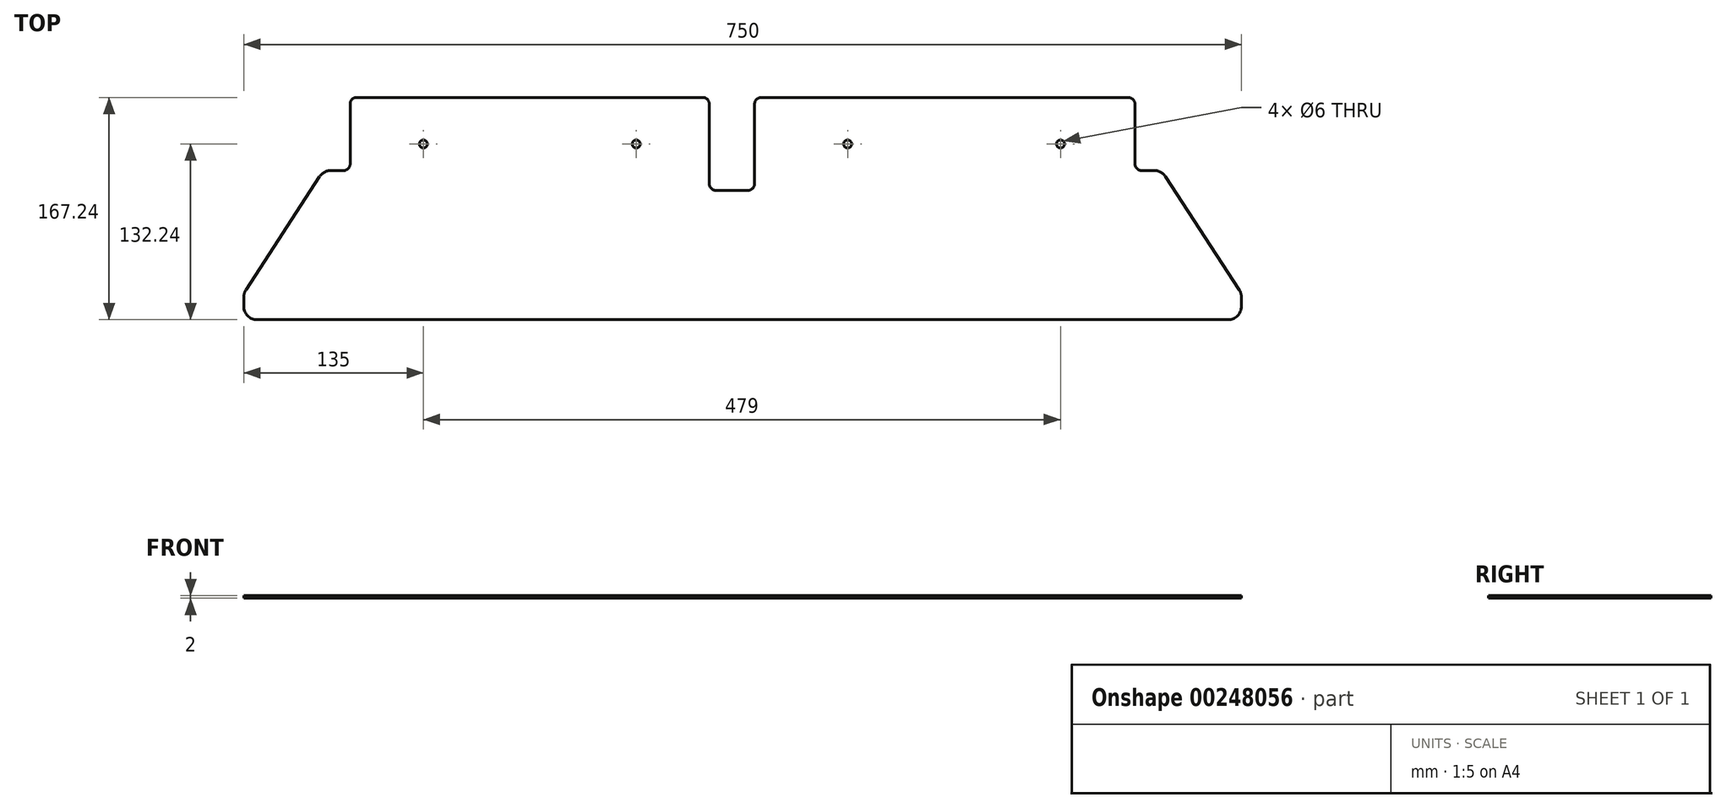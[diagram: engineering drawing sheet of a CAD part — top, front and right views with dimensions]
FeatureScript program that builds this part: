
annotation { "Feature Type Name" : "Feature", "Feature Type Description" : "" }
export const myFeature = defineFeature(function(context is Context, id is Id, definition is map)
    precondition{}
    {
        {
            var Q0;
            Q0=qCreatedBy(makeId("Top.planeOp"),FACE);
            var sketch = newSketch(context, id + "F0", { "sketchPlane" : qUnion([Q0])});
            skLineSegment(sketch, "E0.bottom", {"start": v(5, 0) * mm, "end": v(265, 0) * mm});
            skLineSegment(sketch, "E0.top", {"start": v(0, -55) * mm, "end": v(270, -55) * mm});
            skLineSegment(sketch, "E0.left", {"start": v(0, -5) * mm, "end": v(0, -50) * mm});
            skLineSegment(sketch, "E0.right", {"start": v(590, -5) * mm, "end": v(590, -50) * mm});
            skLineSegment(sketch, "E1", {"start": v(-5, -55) * mm, "end": v(-14.58, -55) * mm});
            skLineSegment(sketch, "E2", {"start": v(595, -55) * mm, "end": v(604.58, -55) * mm});
            skLineSegment(sketch, "E3", {"start": v(-70, -167.24) * mm, "end": v(660, -167.24) * mm});
            skLineSegment(sketch, "E4", {"start": v(-80, -157.24) * mm, "end": v(-80, -150.2) * mm});
            skLineSegment(sketch, "E5", {"start": v(-78.38, -144.75) * mm, "end": v(-22.96, -59.55) * mm});
            skLineSegment(sketch, "E6", {"start": v(670, -157.24) * mm, "end": v(670, -150.2) * mm});
            skLineSegment(sketch, "E7", {"start": v(612.96, -59.55) * mm, "end": v(668.38, -144.75) * mm});
            skLineSegment(sketch, "E8.top", {"start": v(275, -70) * mm, "end": v(299, -70) * mm});
            skLineSegment(sketch, "E8.left", {"start": v(270, -5) * mm, "end": v(270, -65) * mm});
            skLineSegment(sketch, "E8.right", {"start": v(304, -5) * mm, "end": v(304, -65) * mm});
            skPoint(sketch, "E9.visualSharp", {"position": v(270, -70) * mm});
            skArc(sketch, "E9.filletArc", {"start": v(270, -65) * mm, "mid": v(271.46, -68.54) * mm, "end": v(275, -70) * mm});
            skPoint(sketch, "E10.visualSharp", {"position": v(304, -70) * mm});
            skArc(sketch, "E10.filletArc", {"start": v(299, -70) * mm, "mid": v(302.54, -68.54) * mm, "end": v(304, -65) * mm});
            skLineSegment(sketch, "E11.trimOffspring", {"start": v(309, 0) * mm, "end": v(585, 0) * mm});
            skPoint(sketch, "E12.visualSharp", {"position": v(304, 0) * mm});
            skArc(sketch, "E12.filletArc", {"start": v(309, 0) * mm, "mid": v(305.46, -1.46) * mm, "end": v(304, -5) * mm});
            skPoint(sketch, "E13.visualSharp", {"position": v(270, 0) * mm});
            skArc(sketch, "E13.filletArc", {"start": v(270, -5) * mm, "mid": v(268.54, -1.46) * mm, "end": v(265, 0) * mm});
            skPoint(sketch, "E14.visualSharp", {"position": v(590, 0) * mm});
            skArc(sketch, "E14.filletArc", {"start": v(590, -5) * mm, "mid": v(588.54, -1.46) * mm, "end": v(585, 0) * mm});
            skPoint(sketch, "E15.visualSharp", {"position": v(590, -55) * mm});
            skArc(sketch, "E15.filletArc", {"start": v(590, -50) * mm, "mid": v(591.46, -53.54) * mm, "end": v(595, -55) * mm});
            skPoint(sketch, "E16.visualSharp", {"position": v(0, 0) * mm});
            skArc(sketch, "E16.filletArc", {"start": v(5, 0) * mm, "mid": v(1.46, -1.46) * mm, "end": v(0, -5) * mm});
            skPoint(sketch, "E17.visualSharp", {"position": v(0, -55) * mm});
            skArc(sketch, "E17.filletArc", {"start": v(-5, -55) * mm, "mid": v(-1.46, -53.54) * mm, "end": v(0, -50) * mm});
            skPoint(sketch, "E18.visualSharp", {"position": v(-80, -167.24) * mm});
            skArc(sketch, "E18.filletArc", {"start": v(-80, -157.24) * mm, "mid": v(-77.07, -164.31) * mm, "end": v(-70, -167.24) * mm});
            skPoint(sketch, "E19.visualSharp", {"position": v(670, -167.24) * mm});
            skArc(sketch, "E19.filletArc", {"start": v(660, -167.24) * mm, "mid": v(667.07, -164.31) * mm, "end": v(670, -157.24) * mm});
            skLineSegment(sketch, "E20", {"start": v(9.34, -35) * mm, "end": v(270, -35) * mm});
            skCircle(sketch, "E21", {"center": v(55, -35) * mm, "radius": 3 * mm});
            skCircle(sketch, "E22", {"center": v(215, -35) * mm, "radius": 3 * mm});
            skCircle(sketch, "E23", {"center": v(374, -35) * mm, "radius": 3 * mm});
            skCircle(sketch, "E24", {"center": v(534, -35) * mm, "radius": 3 * mm});
            skLineSegment(sketch, "E25.trimOffspring", {"start": v(304, -35) * mm, "end": v(579.75, -35) * mm});
            skLineSegment(sketch, "E26.trimOffspring", {"start": v(304, -55) * mm, "end": v(590, -55) * mm});
            skPoint(sketch, "E27.visualSharp", {"position": v(670, -147.24) * mm});
            skArc(sketch, "E27.filletArc", {"start": v(670, -150.2) * mm, "mid": v(669.59, -147.36) * mm, "end": v(668.38, -144.75) * mm});
            skPoint(sketch, "E28.visualSharp", {"position": v(-80, -147.24) * mm});
            skArc(sketch, "E28.filletArc", {"start": v(-78.38, -144.75) * mm, "mid": v(-79.59, -147.36) * mm, "end": v(-80, -150.2) * mm});
            skPoint(sketch, "E29.visualSharp", {"position": v(-20, -55) * mm});
            skArc(sketch, "E29.filletArc", {"start": v(-14.58, -55) * mm, "mid": v(-19.34, -56.21) * mm, "end": v(-22.96, -59.55) * mm});
            skPoint(sketch, "E30.visualSharp", {"position": v(610, -55) * mm});
            skArc(sketch, "E30.filletArc", {"start": v(612.96, -59.55) * mm, "mid": v(609.34, -56.21) * mm, "end": v(604.58, -55) * mm});
            skSolve(sketch);
        }
        {
            var Q0;
            Q0=makeQuery(id+"F0.imprint","IMPRINT",FACE,{"disambiguationData":[TD([[makeQuery(id+"F0.imprint","IMPRINT",EDGE,{"derivedFrom":sQuery(id+"F0.wireOp",EDGE,"E0.bottom")}),-1.0]])]});
            extrude(context, id + "F1", {"entities" : qUnion([Q0]), "depth" : 2 * mm});
        }
    });
